# Revit family: DBLTD_TheSenatorGroup_Whiteboards_Colab_US
name_source: partatom
category: Furniture
units: mm (PartAtom-declared; Revit-internal decimal feet)

## family parameters
Always vertical = Yes
Cut with Voids When Loaded = No
OmniClass Number = 23.40.20.00
OmniClass Title = General Furniture and Specialties
Room Calculation Point = No
Shared = Yes
Work Plane-Based = No

## types (12) — shared parameters
Assembly Code = E2020200
AssetType = Movable
Category = Pr_40_30_25_96  Whiteboards
Color = Legs; Honey Yellow | Forest Green | Smoke Grey | Ocean Blue. Frame; Smoke Grey. Fabric: Blazer
Constituents = Legs, Frame and Board
DurationUnit = years
ExpectedLife = 5
Finish = Legs; Honey Yellow | Forest Green | Smoke Grey | Ocean Blue. Frame; Smoke Grey. Fabric: Blazer
Keynote = Pr_40_30_25_96  Whiteboards
Manufacturer = The Senator Group
ManufacturerName = The Senator Group
ManufacturerURL = https://www.thesenatorgroup.com
Name = Whiteboards
NominalDepth = 26 "
NominalHeight = 73 "
ProductInformation = https://www.senator.online
Shape = Rectangular
URL = https://www.thesenatorgroup.com
Uniclass2015Code = Pr_40_30_25_96
Uniclass2015Title = Whiteboards
Uniclass2015Version = Products v1.32
Version = 1
WarrantyDescription = The Senator Group warrants that its manufactured products are free from manufacturing defects - in materials or workmanship - for a period of five (5) years.
WarrantyDurationLabor = 5
WarrantyDurationParts = 5
WarrantyDurationUnit = years
WarrantyGuarantorLabor = https://www.thesenatorgroup.com
WarrantyGuarantorParts = https://www.thesenatorgroup.com
zero-valued in all types: Cost, Default Elevation

## per-type parameters (varying)
| type | Material | MediaPlaceHolder | Model | ModelNumber | NominalWidth | Size |
| 49" Drywipe | Legs and Frame; Steel. Board; Drywipe | No | CB7349D | CB7349D | 49 " | 73 x 49 x 26 |
| 65" Drywipe | Legs and Frame; Steel. Board; Drywipe | No | CB7365D | CB7365D | 65 " | 73 x 65 x 26 |
| 65" Pinboard | Legs and Frame; Steel. Board; Pinboard | No | CB7365P | CB7365P | 65 " | 73 x 65 x 26 |
| 49" Pinboard | Legs and Frame; Steel. Board; Pinboard | No | CB7349P | CB7349P | 49 " | 73 x 49 x 26 |
| 49" Magic Drywipe | Legs and Frame; Steel. Board; Magic Drywipe | No | CB7349MD | CB7349MD | 49 " | 73 x 49 x 26 |
| 65" Magic Drywipe | Legs and Frame; Steel. Board; Magic Drywipe | No | CB7365MD | CB7365MD | 65 " | 73 x 65 x 26 |
| 49" Drywipe & Pinboard | Legs and Frame; Steel. Board; Drywipe & Pinboard | No | CB7349DP | CB7349DP | 49 " | 73 x 49 x 26 |
| 49" Magic Drywipe & Pinboard | Legs and Frame; Steel. Board; Magic Drywipe & Pinboard | No | CB7349MDP | CB7349MDP | 49 " | 73 x 49 x 26 |
| 65" Drywipe & Pinboard | Legs and Frame; Steel. Board; Drywipe & Pinboard | No | CB7365DP | CB7365DP | 65 " | 73 x 65 x 26 |
| 65" Magic Drywipe & Pinboard | Legs and Frame; Steel. Board; Magic Drywipe & Pinboard | No | CB7365MDP | CB7365MDP | 65 " | 73 x 65 x 26 |
| 65" Media & Pinboard | Legs and Frame; Steel. Board; Media  & Pinboard | Yes | CB7365PM | CB7365PM | 65 " | 73 x 65 x 26 |
| 49" Media & Pinboard | Legs and Frame; Steel. Board; Media  & Pinboard | Yes | CB7349PM | CB7349PM | 49 " | 73 x 49 x 26 |

note: column(s) folded — value = type name in every type: Description, ModelReference, Type Comments

## geometry (parser evidence)
native form markers: Sweep x6
no freeform markers — native parametric forms only
